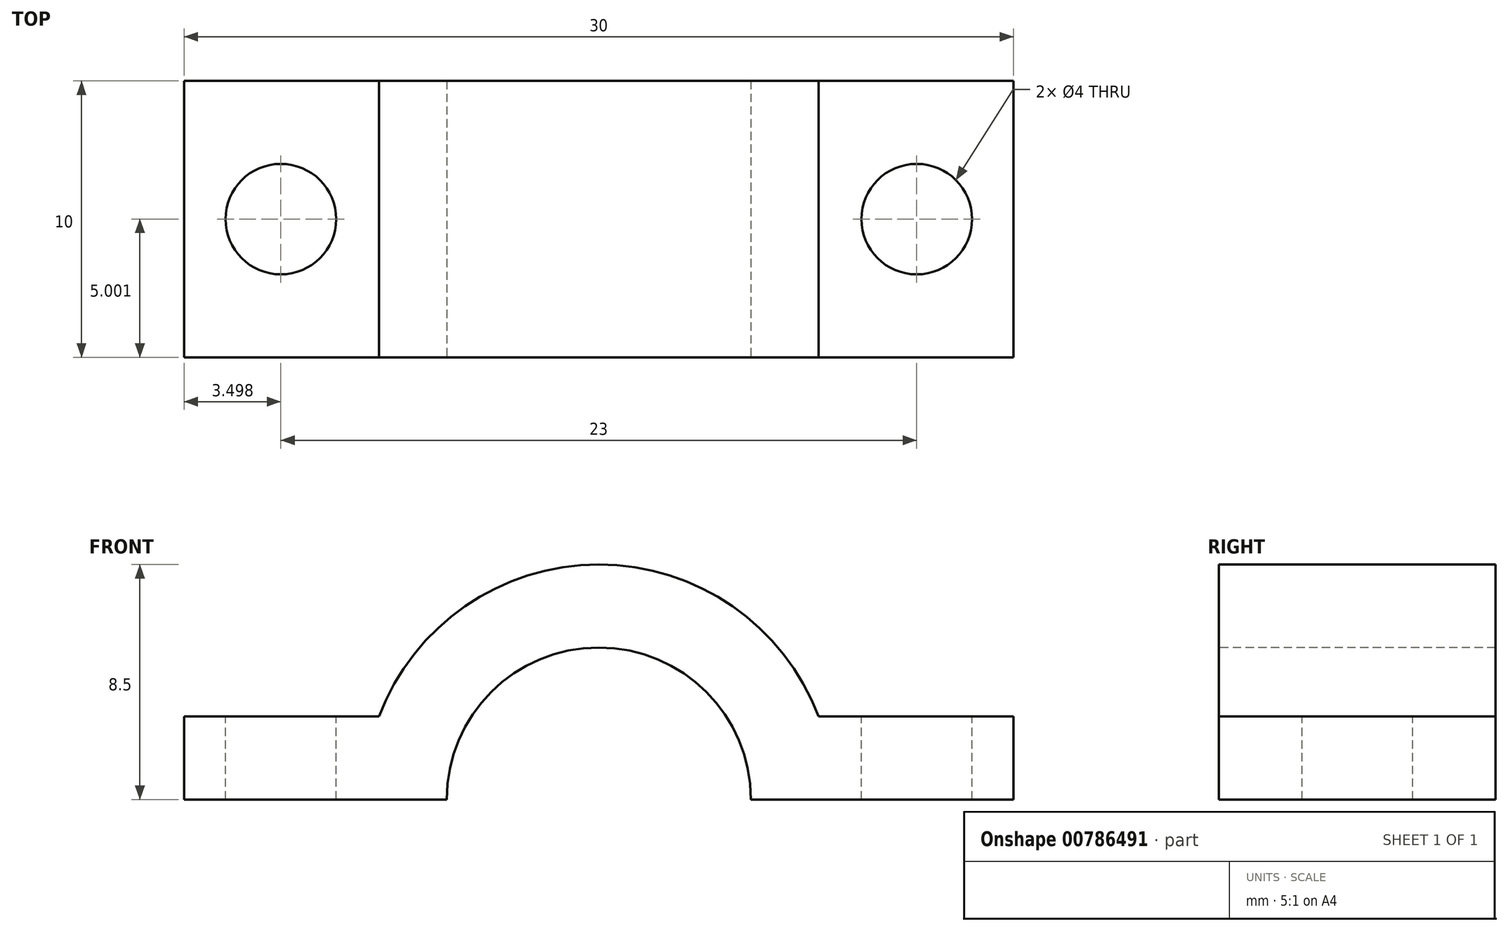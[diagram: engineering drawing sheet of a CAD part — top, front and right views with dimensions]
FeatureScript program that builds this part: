
annotation { "Feature Type Name" : "Feature", "Feature Type Description" : "" }
export const myFeature = defineFeature(function(context is Context, id is Id, definition is map)
    precondition{}
    {
        {
            var Q0;
            Q0=qCreatedBy(makeId("Top.planeOp"),FACE);
            var sketch = newSketch(context, id + "F0", { "sketchPlane" : qUnion([Q0])});
            skLineSegment(sketch, "E0.bottom", {"start": v(-9.15, 6.41) * mm, "end": v(20.85, 6.41) * mm});
            skLineSegment(sketch, "E0.top", {"start": v(-9.15, -3.59) * mm, "end": v(20.85, -3.59) * mm});
            skLineSegment(sketch, "E0.left", {"start": v(-9.15, 6.41) * mm, "end": v(-9.15, -3.59) * mm});
            skLineSegment(sketch, "E0.right", {"start": v(20.85, 6.41) * mm, "end": v(20.85, -3.59) * mm});
            skSolve(sketch);
        }
        {
            var Q0;
            Q0=makeQuery(id+"F0.imprint","IMPRINT",FACE,{"disambiguationData":[TD([[makeQuery(id+"F0.imprint","IMPRINT",EDGE,{"derivedFrom":sQuery(id+"F0.wireOp",EDGE,"E0.bottom")}),-1.0]])]});
            extrude(context, id + "F1", {"entities" : qUnion([Q0]), "depth" : 17 * mm, "offsetDistance" : 25 * mm});
        }
        {
            var Q0;
            Q0=makeQuery(id+"F1.opExtrude","SWEPT_FACE",FACE,{"disambiguationData":[OSD([sQuery(id+"F0.wireOp",EDGE,"E0.top")])]});
            var sketch = newSketch(context, id + "F2", { "sketchPlane" : qUnion([Q0])});
            skCircle(sketch, "E1", {"center": v(5.85, 0) * mm, "radius": 5.5 * mm});
            skCircle(sketch, "E2", {"center": v(5.85, 0) * mm, "radius": 8.5 * mm});
            skLineSegment(sketch, "E3", {"start": v(-9.15, 3) * mm, "end": v(-2.1, 3) * mm});
            skLineSegment(sketch, "E4", {"start": v(13.8, 3) * mm, "end": v(20.85, 3) * mm});
            skSolve(sketch);
        }
        {
            var Q0;
            {var subQ1=sQuery(id+"F2.wireOp",EDGE,"E3");Q0=makeQuery(id+"F2.imprint","IMPRINT",FACE,{"disambiguationData":[TD([[makeQuery(id+"F2.imprint","IMPRINT",EDGE,{"derivedFrom":subQ1}),1.0]])]});}
            var Q1;
            {var subQ0=sQuery(id+"F2.wireOp",EDGE,"E1");var subQ1=makeQuery(id+"F1.opExtrude","CAP_EDGE",EDGE,{"disambiguationData":[OSD([sQuery(id+"F0.wireOp",EDGE,"E0.top")])],"isStart":true});var subQ2=makeQuery(id+"F2.imprint","INTERSECT",VERTEX,{"disambiguationData":[OD(0.0)],"derivedFrom":[subQ1,subQ0]});Q1=makeQuery(id+"F2.imprint","IMPRINT",FACE,{"disambiguationData":[TD([[makeQuery(id+"F2.imprint","IMPRINT",EDGE,{"disambiguationData":[TD([[subQ2,-1.0]])],"derivedFrom":subQ0}),1.0]])]});}
            extrude(context, id + "F3", {"entities" : qUnion([Q0, Q1]), "operationType" : NewBodyOperationType.REMOVE, "oppositeDirection" : true, "depth" : 25 * mm, "offsetDistance" : 25 * mm});
        }
        {
            var Q0;
            Q0=makeQuery(id+"F3.boolean.opBoolean","COPY",FACE,{"derivedFrom":makeQuery(id+"F3.opExtrude","SWEPT_FACE",FACE,{"disambiguationData":[OSD([sQuery(id+"F2.wireOp",EDGE,"E3")])]})});
            var sketch = newSketch(context, id + "F4", { "sketchPlane" : qUnion([Q0])});
            skCircle(sketch, "E5", {"center": v(-5.65, 1.41) * mm, "radius": 2 * mm});
            skCircle(sketch, "E6", {"center": v(17.35, 1.41) * mm, "radius": 2 * mm});
            skLineSegment(sketch, "E7", {"start": v(-9.15, -3.59) * mm, "end": v(-2.1, -3.59) * mm});
            skSolve(sketch);
        }
        {
            var Q0;
            Q0 = qSketchRegion(id + "F4", true);
            extrude(context, id + "F5", {"entities" : qUnion([Q0]), "operationType" : NewBodyOperationType.REMOVE, "oppositeDirection" : true, "depth" : 25 * mm, "offsetDistance" : 25 * mm});
        }
    });
